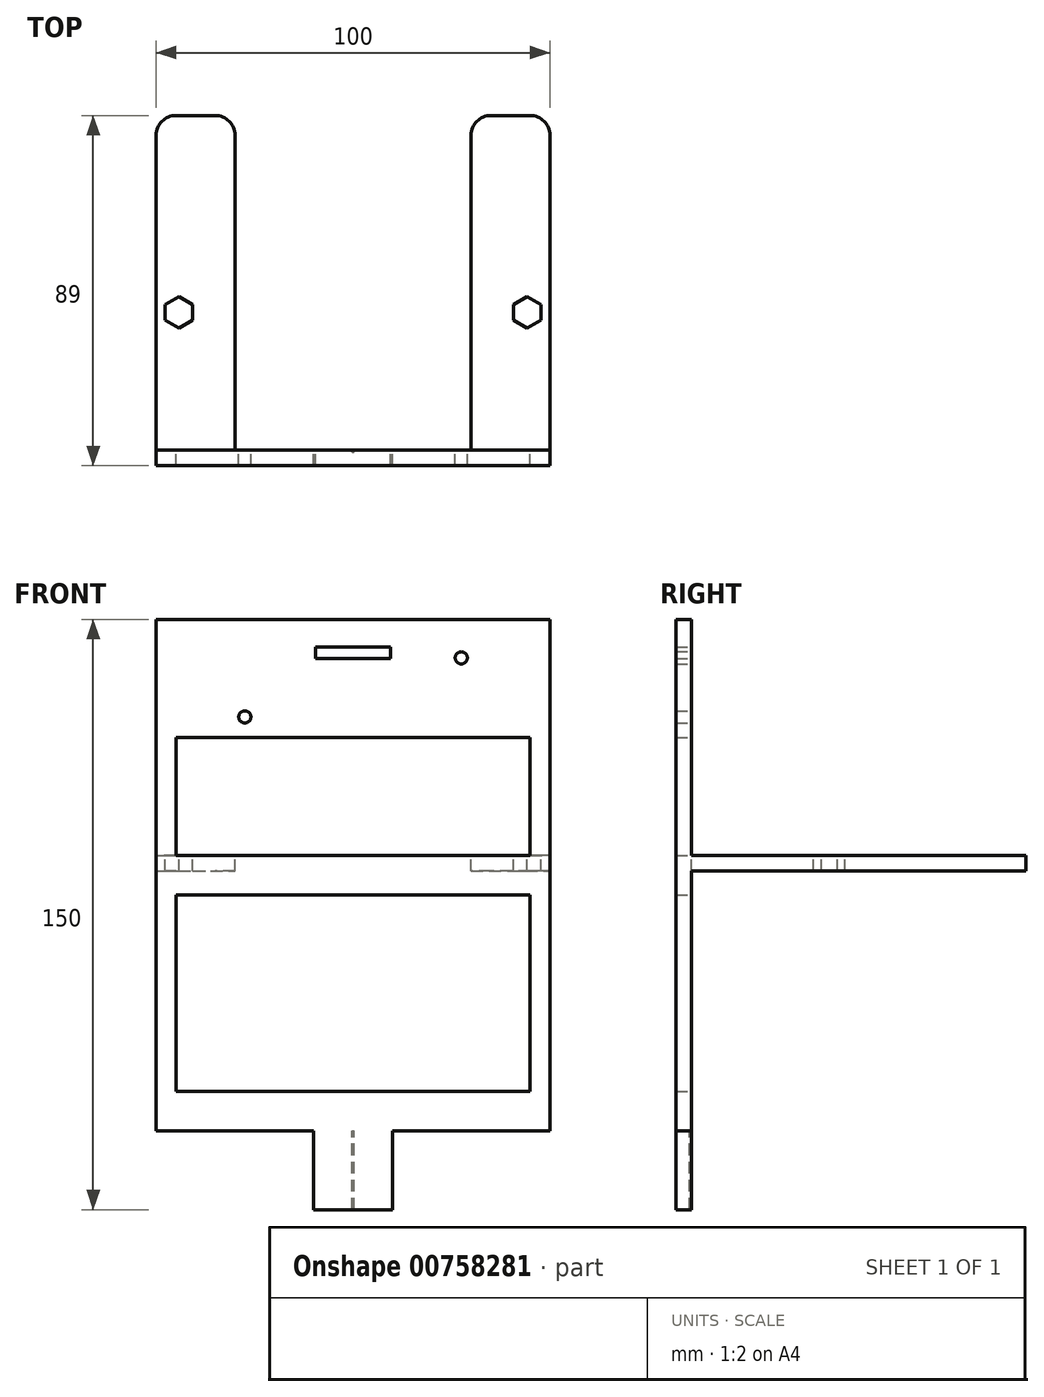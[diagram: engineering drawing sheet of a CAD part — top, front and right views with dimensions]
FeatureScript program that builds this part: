
annotation { "Feature Type Name" : "Feature", "Feature Type Description" : "" }
export const myFeature = defineFeature(function(context is Context, id is Id, definition is map)
    precondition{}
    {
        {
            var Q0;
            Q0=qCreatedBy(makeId("Front.planeOp"),FACE);
            var sketch = newSketch(context, id + "F0", { "sketchPlane" : qUnion([Q0])});
            skLineSegment(sketch, "E0.bottom", {"start": v(-49.14, 66.16) * mm, "end": v(50.86, 66.16) * mm});
            skLineSegment(sketch, "E0.top", {"start": v(-49.14, -83.84) * mm, "end": v(50.86, -83.84) * mm});
            skLineSegment(sketch, "E0.left", {"start": v(-49.14, 66.16) * mm, "end": v(-49.14, -83.84) * mm});
            skLineSegment(sketch, "E0.right", {"start": v(50.86, 66.16) * mm, "end": v(50.86, -83.84) * mm});
            skLineSegment(sketch, "E1.bottom", {"start": v(50.86, -83.84) * mm, "end": v(10.86, -83.84) * mm});
            skLineSegment(sketch, "E1.top", {"start": v(50.86, -63.84) * mm, "end": v(10.86, -63.84) * mm});
            skLineSegment(sketch, "E1.left", {"start": v(50.86, -83.84) * mm, "end": v(50.86, -63.84) * mm});
            skLineSegment(sketch, "E1.right", {"start": v(10.86, -83.84) * mm, "end": v(10.86, -63.84) * mm});
            skLineSegment(sketch, "E2.bottom", {"start": v(-49.14, -83.84) * mm, "end": v(-9.14, -83.84) * mm});
            skLineSegment(sketch, "E2.top", {"start": v(-49.14, -63.84) * mm, "end": v(-9.14, -63.84) * mm});
            skLineSegment(sketch, "E2.left", {"start": v(-49.14, -83.84) * mm, "end": v(-49.14, -63.84) * mm});
            skLineSegment(sketch, "E2.right", {"start": v(-9.14, -83.84) * mm, "end": v(-9.14, -63.84) * mm});
            skLineSegment(sketch, "E3.bottom", {"start": v(-44.14, -3.84) * mm, "end": v(45.86, -3.84) * mm});
            skLineSegment(sketch, "E3.top", {"start": v(-44.14, -53.84) * mm, "end": v(45.86, -53.84) * mm});
            skLineSegment(sketch, "E3.left", {"start": v(-44.14, -3.84) * mm, "end": v(-44.14, -53.84) * mm});
            skLineSegment(sketch, "E3.right", {"start": v(45.86, -3.84) * mm, "end": v(45.86, -53.84) * mm});
            skLineSegment(sketch, "E4.bottom", {"start": v(-44.14, 36.16) * mm, "end": v(45.86, 36.16) * mm});
            skLineSegment(sketch, "E4.top", {"start": v(-44.14, 6.16) * mm, "end": v(45.86, 6.16) * mm});
            skLineSegment(sketch, "E4.left", {"start": v(-44.14, 36.16) * mm, "end": v(-44.14, 6.16) * mm});
            skLineSegment(sketch, "E4.right", {"start": v(45.86, 36.16) * mm, "end": v(45.86, 6.16) * mm});
            skLineSegment(sketch, "E5.bottom", {"start": v(10.36, 56.16) * mm, "end": v(-8.64, 56.16) * mm});
            skLineSegment(sketch, "E5.top", {"start": v(10.36, 59.16) * mm, "end": v(-8.64, 59.16) * mm});
            skLineSegment(sketch, "E5.left", {"start": v(10.36, 56.16) * mm, "end": v(10.36, 59.16) * mm});
            skLineSegment(sketch, "E5.right", {"start": v(-8.64, 56.16) * mm, "end": v(-8.64, 59.16) * mm});
            skCircle(sketch, "E6", {"center": v(28.36, 56.36) * mm, "radius": 1.55 * mm});
            skCircle(sketch, "E7", {"center": v(-26.64, 41.36) * mm, "radius": 1.55 * mm});
            skSolve(sketch);
        }
        {
            var Q0;
            Q0=makeQuery(id+"F0.imprint","IMPRINT",FACE,{"disambiguationData":[TD([[makeQuery(id+"F0.imprint","IMPRINT",EDGE,{"derivedFrom":sQuery(id+"F0.wireOp",EDGE,"E0.bottom")}),-1.0]])]});
            extrude(context, id + "F1", {"entities" : qUnion([Q0]), "depth" : 4 * mm, "offsetDistance" : 25 * mm});
        }
        {
            var Q0;
            Q0=makeQuery(id+"F1.opExtrude","SWEPT_FACE",FACE,{"disambiguationData":[OSD([sQuery(id+"F0.wireOp",EDGE,"E4.top")])]});
            var sketch = newSketch(context, id + "F2", { "sketchPlane" : qUnion([Q0])});
            skLineSegment(sketch, "E8.0", {"start": v(-49.14, 0) * mm, "end": v(50.86, 0) * mm});
            skLineSegment(sketch, "E9.bottom", {"start": v(-49.14, 0) * mm, "end": v(-29.14, 0) * mm});
            skLineSegment(sketch, "E9.top", {"start": v(-44.14, 85) * mm, "end": v(-34.14, 85) * mm});
            skLineSegment(sketch, "E9.left", {"start": v(-49.14, 0) * mm, "end": v(-49.14, 80) * mm});
            skLineSegment(sketch, "E9.right", {"start": v(-29.14, 0) * mm, "end": v(-29.14, 80) * mm});
            skLineSegment(sketch, "E10.bottom", {"start": v(45.86, 85) * mm, "end": v(35.86, 85) * mm});
            skLineSegment(sketch, "E10.top", {"start": v(50.86, 0) * mm, "end": v(30.86, 0) * mm});
            skLineSegment(sketch, "E10.left", {"start": v(50.86, 80) * mm, "end": v(50.86, 0) * mm});
            skLineSegment(sketch, "E10.right", {"start": v(30.86, 80) * mm, "end": v(30.86, 0) * mm});
            skPoint(sketch, "E11.visualSharp", {"position": v(-49.14, 85) * mm});
            skArc(sketch, "E11.filletArc", {"start": v(-44.14, 85) * mm, "mid": v(-47.68, 83.54) * mm, "end": v(-49.14, 80) * mm});
            skPoint(sketch, "E12.visualSharp", {"position": v(-29.14, 85) * mm});
            skArc(sketch, "E12.filletArc", {"start": v(-29.14, 80) * mm, "mid": v(-30.6, 83.54) * mm, "end": v(-34.14, 85) * mm});
            skPoint(sketch, "E13.visualSharp", {"position": v(50.86, 85) * mm});
            skArc(sketch, "E13.filletArc", {"start": v(50.86, 80) * mm, "mid": v(49.4, 83.54) * mm, "end": v(45.86, 85) * mm});
            skPoint(sketch, "E14.visualSharp", {"position": v(30.86, 85) * mm});
            skArc(sketch, "E14.filletArc", {"start": v(35.86, 85) * mm, "mid": v(32.32, 83.54) * mm, "end": v(30.86, 80) * mm});
            skCircle(sketch, "E15.cCircle", {"center": v(-43.4, 35) * mm, "radius": 3.46 * mm, "construction": true});
            skLineSegment(sketch, "E15.0", {"start": v(-43.4, 39) * mm, "end": v(-39.93, 37) * mm});
            skLineSegment(sketch, "E15.1", {"start": v(-39.93, 37) * mm, "end": v(-39.93, 33) * mm});
            skLineSegment(sketch, "E15.2", {"start": v(-39.93, 33) * mm, "end": v(-43.4, 31) * mm});
            skLineSegment(sketch, "E15.3", {"start": v(-43.4, 31) * mm, "end": v(-46.85, 33) * mm});
            skLineSegment(sketch, "E15.4", {"start": v(-46.85, 33) * mm, "end": v(-46.85, 37) * mm});
            skLineSegment(sketch, "E15.5", {"start": v(-46.85, 37) * mm, "end": v(-43.4, 39) * mm});
            skPoint(sketch, "E15.0.midPoint", {"position": v(-41.66, 38) * mm});
            skLineSegment(sketch, "E16", {"start": v(0.86, -4) * mm, "end": v(0.86, 92.09) * mm, "construction": true});
            skCircle(sketch, "E17.MirrorC", {"center": v(45.1, 35) * mm, "radius": 3.46 * mm, "construction": true});
            skLineSegment(sketch, "E18.MirrorCS", {"start": v(48.57, 37) * mm, "end": v(45.1, 39) * mm});
            skLineSegment(sketch, "E19.MirrorCS", {"start": v(45.1, 39) * mm, "end": v(41.65, 37) * mm});
            skLineSegment(sketch, "E20.MirrorCS", {"start": v(41.65, 37) * mm, "end": v(41.65, 33) * mm});
            skLineSegment(sketch, "E21.MirrorCS", {"start": v(41.65, 33) * mm, "end": v(45.1, 31) * mm});
            skLineSegment(sketch, "E22.MirrorCS", {"start": v(45.1, 31) * mm, "end": v(48.57, 33) * mm});
            skLineSegment(sketch, "E23.MirrorCS", {"start": v(48.57, 33) * mm, "end": v(48.57, 37) * mm});
            skSolve(sketch);
        }
        {
            var Q0;
            Q0=qSketchRegion(id+"F2",true);
            extrude(context, id + "F3", {"entities" : qUnion([Q0]), "operationType" : NewBodyOperationType.ADD, "oppositeDirection" : true, "depth" : 4 * mm, "offsetDistance" : 25 * mm});
        }
        {
            var Q0;
            {var subQ0=sQuery(id+"F0.wireOp",EDGE,"E3.left");var subQ13=sQuery(id+"F0.wireOp",EDGE,"E3.top");var subQ14=sQuery(id+"F0.wireOp",EDGE,"E3.bottom");var subQ15=sQuery(id+"F0.wireOp",EDGE,"E2.right");var subQ17=sQuery(id+"F0.wireOp",EDGE,"E2.top");var subQ19=sQuery(id+"F0.wireOp",EDGE,"E1.right");var subQ20=sQuery(id+"F0.wireOp",EDGE,"E0.top");var subQ21=sQuery(id+"F0.wireOp",EDGE,"E0.left");var subQ22=sQuery(id+"F0.wireOp",EDGE,"E0.right");var subQ33=sQuery(id+"F0.wireOp",EDGE,"E1.top");var subQ34=sQuery(id+"F0.wireOp",EDGE,"E3.right");var subQ35=sQuery(id+"F0.wireOp",EDGE,"E4.top");Q0=makeQuery(id+"F3.boolean.opBoolean","SPLIT",FACE,{"disambiguationData":[TD([makeQuery(id+"F1.opExtrude","SWEPT_FACE",FACE,{"disambiguationData":[OSD([subQ20])]})])],"derivedFrom":makeQuery(id+"F1.opExtrude","CAP_FACE",FACE,{"disambiguationData":[OSD([sQuery(id+"F0.wireOp",EDGE,"E0.bottom"),subQ20,subQ21,subQ22,subQ33,subQ19,subQ17,subQ15,subQ14,subQ13,subQ0,subQ34,sQuery(id+"F0.wireOp",EDGE,"E4.bottom"),subQ35,sQuery(id+"F0.wireOp",EDGE,"E4.left"),sQuery(id+"F0.wireOp",EDGE,"E4.right"),sQuery(id+"F0.wireOp",EDGE,"E5.bottom"),sQuery(id+"F0.wireOp",EDGE,"E5.top"),sQuery(id+"F0.wireOp",EDGE,"E5.left"),sQuery(id+"F0.wireOp",EDGE,"E5.right"),sQuery(id+"F0.wireOp",EDGE,"E6"),sQuery(id+"F0.wireOp",EDGE,"E7")])],"isStart":true})});}
            var sketch = newSketch(context, id + "F4", { "sketchPlane" : qUnion([Q0])});
            skLineSegment(sketch, "E24.bottom", {"start": v(-1.1, -53.84) * mm, "end": v(-0.6, -53.84) * mm});
            skLineSegment(sketch, "E24.top", {"start": v(-1.1, -83.84) * mm, "end": v(-0.6, -83.84) * mm});
            skLineSegment(sketch, "E25.bottom", {"start": v(-0.6, -83.84) * mm, "end": v(-1.1, -83.84) * mm});
            skLineSegment(sketch, "E25.top", {"start": v(-0.6, -63.84) * mm, "end": v(-1.1, -63.84) * mm});
            skLineSegment(sketch, "E25.left", {"start": v(-0.6, -83.84) * mm, "end": v(-0.6, -63.84) * mm});
            skLineSegment(sketch, "E25.right", {"start": v(-1.1, -83.84) * mm, "end": v(-1.1, -63.84) * mm});
            skSolve(sketch);
        }
        {
            var Q0;
            Q0=qSketchRegion(id+"F4",true);
            extrude(context, id + "F5", {"entities" : qUnion([Q0]), "operationType" : NewBodyOperationType.REMOVE, "oppositeDirection" : true, "depth" : 0.5 * mm, "offsetDistance" : 25 * mm});
        }
    });
